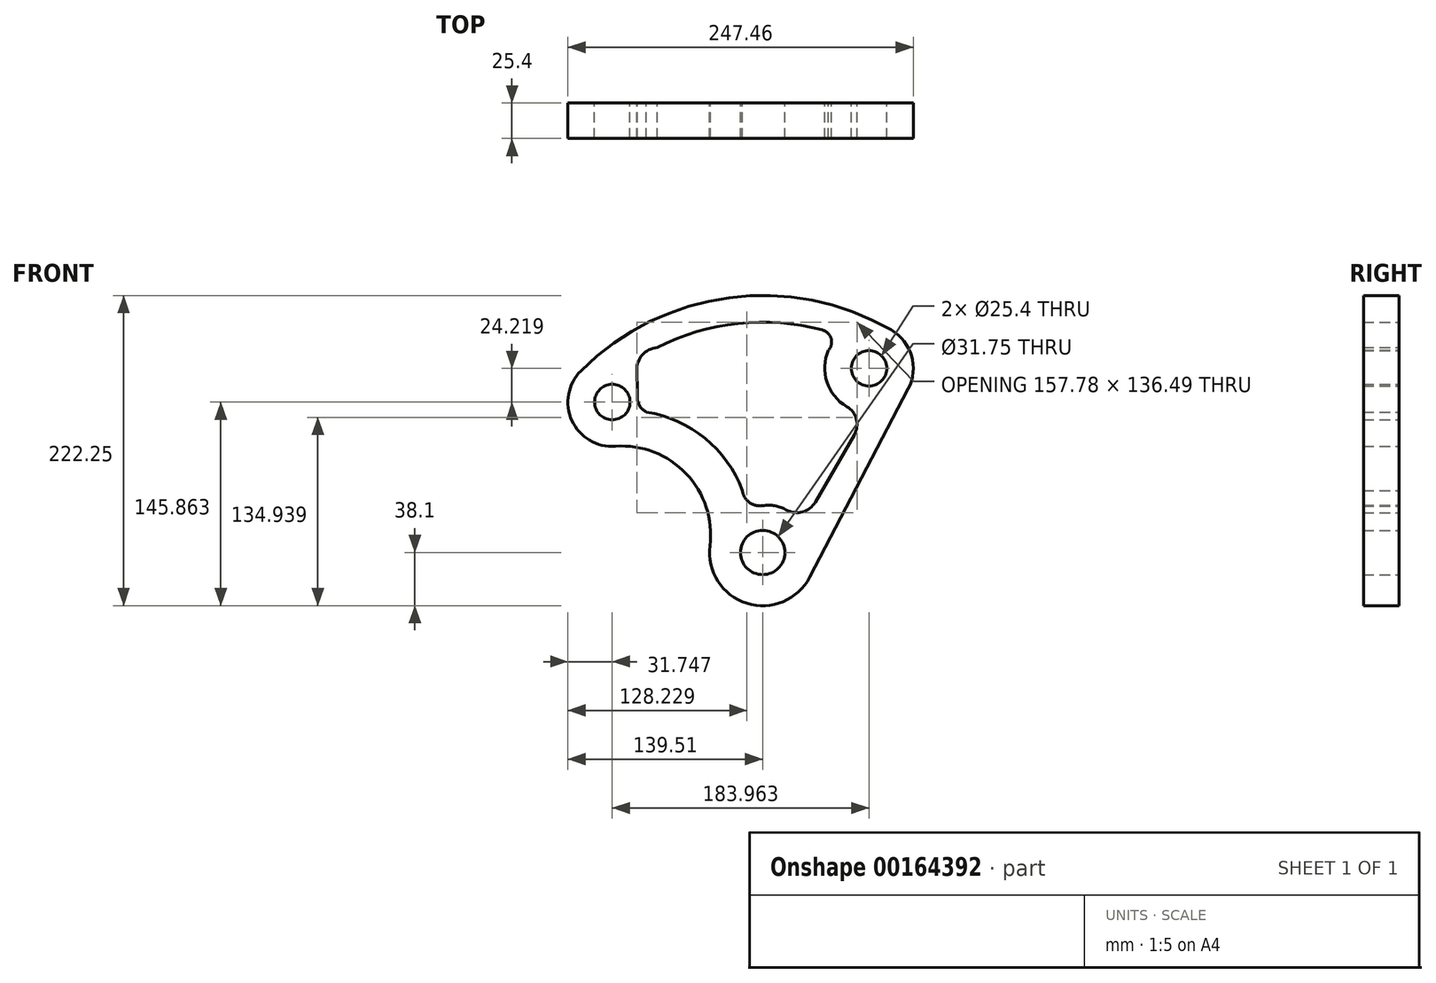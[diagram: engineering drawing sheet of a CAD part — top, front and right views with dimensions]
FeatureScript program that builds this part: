
annotation { "Feature Type Name" : "Feature", "Feature Type Description" : "" }
export const myFeature = defineFeature(function(context is Context, id is Id, definition is map)
    precondition{}
    {
        {
            var Q0;
            Q0=qCreatedBy(makeId("Front.planeOp"),FACE);
            var sketch = newSketch(context, id + "F0", { "sketchPlane" : qUnion([Q0])});
            skCircle(sketch, "E0", {"center": v(0, 0) * mm, "radius": 15.88 * mm});
            skLineSegment(sketch, "E1", {"start": v(0, 0) * mm, "end": v(0, 159.48) * mm});
            skLineSegment(sketch, "E2", {"start": v(0, 0) * mm, "end": v(92.08, 159.48) * mm, "construction": true});
            skLineSegment(sketch, "E3", {"start": v(0, 0) * mm, "end": v(-159.48, 159.48) * mm, "construction": true});
            skCircle(sketch, "E4", {"center": v(76.2, 131.98) * mm, "radius": 12.7 * mm});
            skCircle(sketch, "E5", {"center": v(-107.76, 107.76) * mm, "radius": 12.7 * mm});
            skLineSegment(sketch, "E6", {"start": v(38.1, 0) * mm, "end": v(-37.8, 4.79) * mm, "construction": true});
            skArc(sketch, "E7", {"start": v(76.2, 131.98) * mm, "mid": v(-19.9, 151.1) * mm, "end": v(-107.76, 107.76) * mm, "construction": true});
            skLineSegment(sketch, "E8", {"start": v(0, 0) * mm, "end": v(0, -38.1) * mm, "construction": true});
            skArc(sketch, "E9", {"start": v(-37.8, 4.79) * mm, "mid": v(-28.58, -25.2) * mm, "end": v(0, -38.1) * mm});
            skArc(sketch, "E10", {"start": v(0, -38.1) * mm, "mid": v(26.94, -26.94) * mm, "end": v(38.1, 0) * mm});
            skLineSegment(sketch, "E11", {"start": v(33.76, -17.66) * mm, "end": v(104.33, 117.27) * mm});
            skArc(sketch, "E12", {"start": v(104.33, 117.27) * mm, "mid": v(106.7, 140.84) * mm, "end": v(92.08, 159.48) * mm});
            skArc(sketch, "E13", {"start": v(92.08, 159.48) * mm, "mid": v(-24.04, 182.57) * mm, "end": v(-130.21, 130.21) * mm});
            skArc(sketch, "E14", {"start": v(-130.21, 130.21) * mm, "mid": v(-139.51, 107.76) * mm, "end": v(-130.21, 85.31) * mm});
            skArc(sketch, "E15", {"start": v(-130.21, 85.31) * mm, "mid": v(-118.83, 78) * mm, "end": v(-105.44, 76.1) * mm});
            skArc(sketch, "E16", {"start": v(-37.8, 4.79) * mm, "mid": v(-54.72, 56.47) * mm, "end": v(-105.44, 76.1) * mm});
            skArc(sketch, "E17", {"start": v(47.2, 144.9) * mm, "mid": v(46, 122.18) * mm, "end": v(60.33, 104.49) * mm});
            skArc(sketch, "E18", {"start": v(47.2, 144.9) * mm, "mid": v(48.99, 153.43) * mm, "end": v(42.72, 159.48) * mm});
            skArc(sketch, "E19", {"start": v(42.72, 159.48) * mm, "mid": v(-17.62, 164.16) * mm, "end": v(-75.58, 146.78) * mm});
            skArc(sketch, "E20", {"start": v(-75.58, 146.78) * mm, "mid": v(-86.18, 141.6) * mm, "end": v(-90.17, 130.5) * mm});
            skArc(sketch, "E21", {"start": v(60.33, 104.49) * mm, "mid": v(67.14, 95.6) * mm, "end": v(65.68, 84.5) * mm});
            skLineSegment(sketch, "E22", {"start": v(65.68, 84.5) * mm, "end": v(37.82, 36.24) * mm});
            skArc(sketch, "E23", {"start": v(17.01, 30.5) * mm, "mid": v(28.6, 29.1) * mm, "end": v(37.82, 36.24) * mm});
            skArc(sketch, "E24", {"start": v(17.01, 30.5) * mm, "mid": v(8.76, 33.45) * mm, "end": v(0, 33.55) * mm});
            skArc(sketch, "E25", {"start": v(-89.89, 111.55) * mm, "mid": v(-88.17, 105.16) * mm, "end": v(-83.38, 100.6) * mm});
            skArc(sketch, "E26", {"start": v(-14.54, 44.42) * mm, "mid": v(-41.27, 81.94) * mm, "end": v(-83.38, 100.6) * mm});
            skArc(sketch, "E27", {"start": v(-89.89, 111.55) * mm, "mid": v(-89.9, 121.03) * mm, "end": v(-90.17, 130.5) * mm});
            skArc(sketch, "E28", {"start": v(-14.54, 44.42) * mm, "mid": v(-9.56, 35.93) * mm, "end": v(0, 33.55) * mm});
            skSolve(sketch);
        }
        {
            var Q0;
            Q0=makeQuery(id+"F0.imprint","IMPRINT",FACE,{"disambiguationData":[TD([[makeQuery(id+"F0.imprint","IMPRINT",EDGE,{"derivedFrom":sQuery(id+"F0.wireOp",EDGE,"E0")}),-1.0]])]});
            extrude(context, id + "F1", {"entities" : qUnion([Q0]), "depth" : 25.4 * mm});
        }
    });
